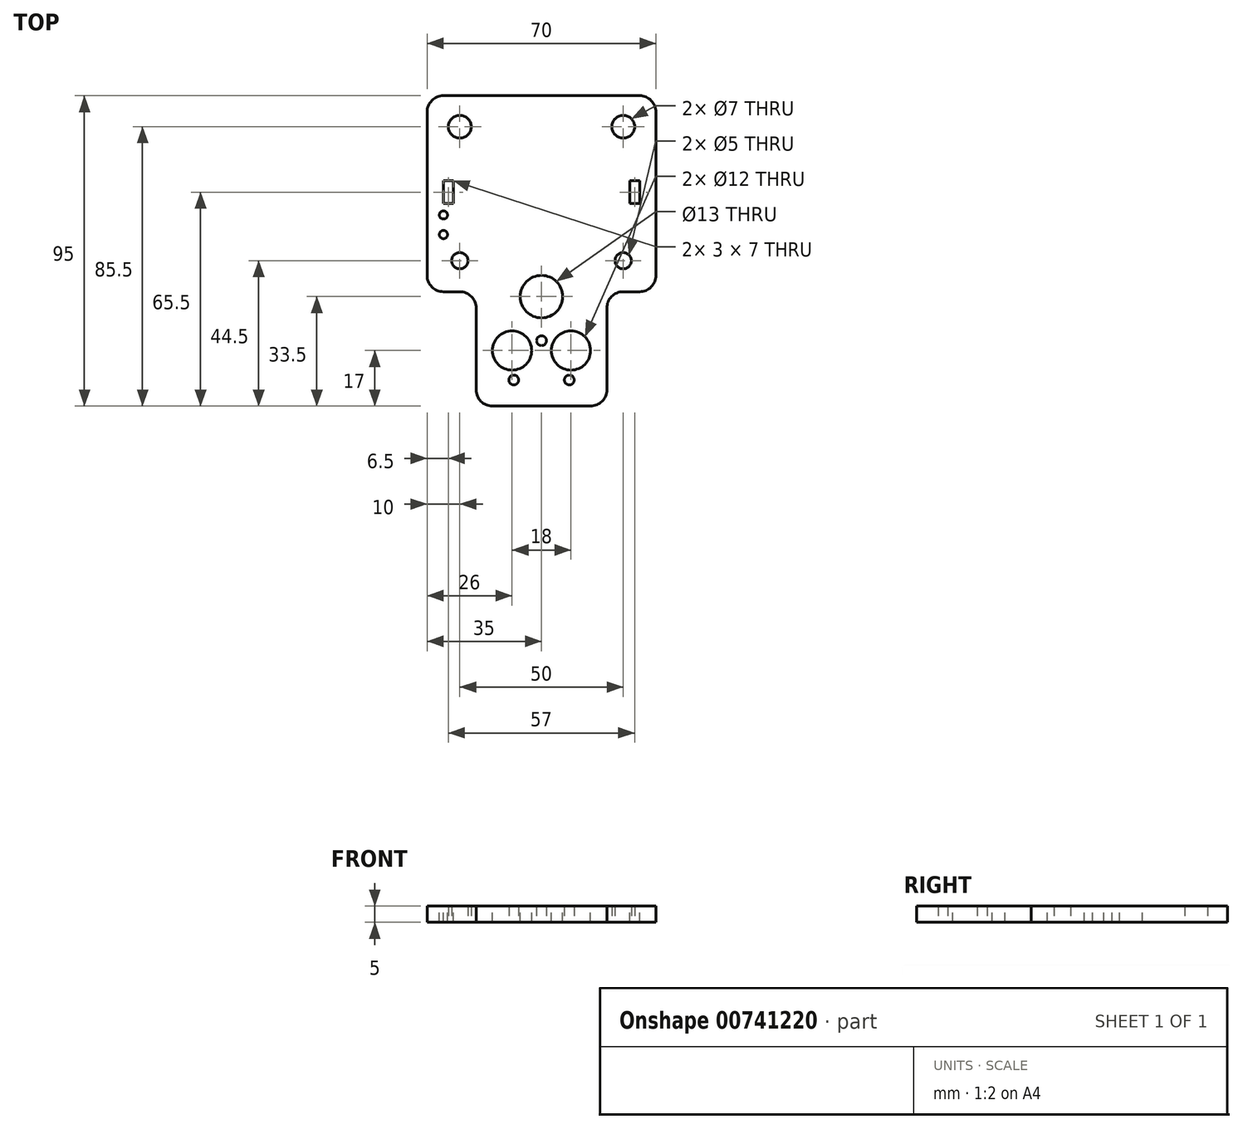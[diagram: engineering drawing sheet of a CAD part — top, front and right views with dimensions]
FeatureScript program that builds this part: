
annotation { "Feature Type Name" : "Feature", "Feature Type Description" : "" }
export const myFeature = defineFeature(function(context is Context, id is Id, definition is map)
    precondition{}
    {
        {
            var Q0;
            Q0=qCreatedBy(makeId("Top.planeOp"),FACE);
            var sketch = newSketch(context, id + "F0", { "sketchPlane" : qUnion([Q0])});
            skLineSegment(sketch, "E0.bottom", {"start": v(35, 30) * mm, "end": v(-35, 30) * mm});
            skLineSegment(sketch, "E0.top", {"start": v(35, -30) * mm, "end": v(-35, -30) * mm});
            skLineSegment(sketch, "E0.left", {"start": v(35, 30) * mm, "end": v(35, -30) * mm});
            skLineSegment(sketch, "E0.right", {"start": v(-35, 30) * mm, "end": v(-35, -30) * mm});
            skPoint(sketch, "E0.middle", {"position": v(0, 0) * mm});
            skLineSegment(sketch, "E1.bottom", {"start": v(20, -30) * mm, "end": v(-20, -30) * mm});
            skLineSegment(sketch, "E1.top", {"start": v(20, -65) * mm, "end": v(-20, -65) * mm});
            skLineSegment(sketch, "E1.left", {"start": v(20, -30) * mm, "end": v(20, -65) * mm});
            skLineSegment(sketch, "E1.right", {"start": v(-20, -30) * mm, "end": v(-20, -65) * mm});
            skPoint(sketch, "E1.middle", {"position": v(0, -47.5) * mm});
            skLineSegment(sketch, "E2.bottom", {"start": v(25, 20.5) * mm, "end": v(-25, 20.5) * mm, "construction": true});
            skLineSegment(sketch, "E2.top", {"start": v(25, -20.5) * mm, "end": v(-25, -20.5) * mm, "construction": true});
            skLineSegment(sketch, "E2.left", {"start": v(25, 20.5) * mm, "end": v(25, -20.5) * mm, "construction": true});
            skLineSegment(sketch, "E2.right", {"start": v(-25, 20.5) * mm, "end": v(-25, -20.5) * mm, "construction": true});
            skCircle(sketch, "E3", {"center": v(-25, 20.5) * mm, "radius": 3.5 * mm});
            skCircle(sketch, "E4", {"center": v(25, 20.5) * mm, "radius": 3.5 * mm});
            skCircle(sketch, "E5", {"center": v(-25, -20.5) * mm, "radius": 2.5 * mm});
            skCircle(sketch, "E6", {"center": v(25, -20.5) * mm, "radius": 2.5 * mm});
            skLineSegment(sketch, "E7", {"start": v(0, -65) * mm, "end": v(0, 30) * mm, "construction": true});
            skLineSegment(sketch, "E8", {"start": v(-20, -57) * mm, "end": v(20, -57) * mm, "construction": true});
            skCircle(sketch, "E9", {"center": v(-8.5, -57) * mm, "radius": 1.5 * mm});
            skCircle(sketch, "E10", {"center": v(8.5, -57) * mm, "radius": 1.5 * mm});
            skCircle(sketch, "E11", {"center": v(0, -45) * mm, "radius": 1.5 * mm});
            skSolve(sketch);
        }
        {
            var Q0;
            Q0 = qSketchRegion(id + "F0", true);
            extrude(context, id + "F1", {"entities" : qUnion([Q0]), "depth" : 5 * mm, "offsetDistance" : 25 * mm});
        }
        {
            var Q0;
            Q0=makeQuery(id+"F1.opExtrude","CAP_FACE",FACE,{"disambiguationData":[OSD([sQuery(id+"F0.wireOp",EDGE,"E0.bottom"),sQuery(id+"F0.wireOp",EDGE,"E0.top"),sQuery(id+"F0.wireOp",EDGE,"E0.left"),sQuery(id+"F0.wireOp",EDGE,"E0.right"),sQuery(id+"F0.wireOp",EDGE,"E1.top"),sQuery(id+"F0.wireOp",EDGE,"E1.left"),sQuery(id+"F0.wireOp",EDGE,"E1.right"),sQuery(id+"F0.wireOp",EDGE,"E3"),sQuery(id+"F0.wireOp",EDGE,"E4"),sQuery(id+"F0.wireOp",EDGE,"E5"),sQuery(id+"F0.wireOp",EDGE,"E6"),sQuery(id+"F0.wireOp",EDGE,"E9"),sQuery(id+"F0.wireOp",EDGE,"E10"),sQuery(id+"F0.wireOp",EDGE,"E11")])],"isStart":false});
            var sketch = newSketch(context, id + "F2", { "sketchPlane" : qUnion([Q0])});
            skLineSegment(sketch, "E12", {"start": v(0, 30) * mm, "end": v(0, -65) * mm, "construction": true});
            skLineSegment(sketch, "E13", {"start": v(-20, -48) * mm, "end": v(20, -48) * mm, "construction": true});
            skCircle(sketch, "E14", {"center": v(-9, -48) * mm, "radius": 6 * mm});
            skCircle(sketch, "E15", {"center": v(9, -48) * mm, "radius": 6 * mm});
            skCircle(sketch, "E16", {"center": v(0, -31.5) * mm, "radius": 6.5 * mm});
            skSolve(sketch);
        }
        {
            var Q0;
            Q0 = qSketchRegion(id + "F2", true);
            extrude(context, id + "F3", {"entities" : qUnion([Q0]), "operationType" : NewBodyOperationType.REMOVE, "endBound" : BoundingType.THROUGH_ALL, "oppositeDirection" : true, "depth" : 25 * mm, "offsetDistance" : 25 * mm});
        }
        {
            var Q0;
            Q0=makeQuery(id+"F1.opExtrude","CAP_FACE",FACE,{"disambiguationData":[OSD([sQuery(id+"F0.wireOp",EDGE,"E0.bottom"),sQuery(id+"F0.wireOp",EDGE,"E0.top"),sQuery(id+"F0.wireOp",EDGE,"E0.left"),sQuery(id+"F0.wireOp",EDGE,"E0.right"),sQuery(id+"F0.wireOp",EDGE,"E1.top"),sQuery(id+"F0.wireOp",EDGE,"E1.left"),sQuery(id+"F0.wireOp",EDGE,"E1.right"),sQuery(id+"F0.wireOp",EDGE,"E3"),sQuery(id+"F0.wireOp",EDGE,"E4"),sQuery(id+"F0.wireOp",EDGE,"E5"),sQuery(id+"F0.wireOp",EDGE,"E6"),sQuery(id+"F0.wireOp",EDGE,"E9"),sQuery(id+"F0.wireOp",EDGE,"E10"),sQuery(id+"F0.wireOp",EDGE,"E11")])],"isStart":false});
            var sketch = newSketch(context, id + "F4", { "sketchPlane" : qUnion([Q0])});
            skLineSegment(sketch, "E17.bottom", {"start": v(30, -3) * mm, "end": v(27, -3) * mm});
            skLineSegment(sketch, "E17.top", {"start": v(30, 4) * mm, "end": v(27, 4) * mm});
            skLineSegment(sketch, "E17.left", {"start": v(30, -3) * mm, "end": v(30, 4) * mm});
            skLineSegment(sketch, "E17.right", {"start": v(27, -3) * mm, "end": v(27, 4) * mm});
            skPoint(sketch, "E17.middle", {"position": v(28.5, 0.5) * mm});
            skLineSegment(sketch, "E18.bottom", {"start": v(-27, 4) * mm, "end": v(-30, 4) * mm});
            skLineSegment(sketch, "E18.top", {"start": v(-27, -3) * mm, "end": v(-30, -3) * mm});
            skLineSegment(sketch, "E18.left", {"start": v(-27, 4) * mm, "end": v(-27, -3) * mm});
            skLineSegment(sketch, "E18.right", {"start": v(-30, 4) * mm, "end": v(-30, -3) * mm});
            skPoint(sketch, "E18.middle", {"position": v(-28.5, 0.5) * mm});
            skLineSegment(sketch, "E19", {"start": v(0, 30) * mm, "end": v(0, -65) * mm, "construction": true});
            skSolve(sketch);
        }
        {
            var Q0;
            Q0 = qSketchRegion(id + "F4", true);
            extrude(context, id + "F5", {"entities" : qUnion([Q0]), "operationType" : NewBodyOperationType.REMOVE, "endBound" : BoundingType.THROUGH_ALL, "oppositeDirection" : true, "depth" : 25 * mm, "offsetDistance" : 25 * mm});
        }
        {
            var Q0;
            Q0=makeQuery(id+"F2.imprint","IMPRINT",FACE,{"disambiguationData":[TD([[makeQuery(id+"F2.imprint","IMPRINT",EDGE,{"derivedFrom":sQuery(id+"F2.wireOp",EDGE,"E14")}),-1.0]])]});
            var sketch = newSketch(context, id + "F6", { "sketchPlane" : qUnion([Q0])});
            skLineSegment(sketch, "E20", {"start": v(-30, -6.5) * mm, "end": v(-30, -12.5) * mm, "construction": true});
            skCircle(sketch, "E21", {"center": v(-30, -6.5) * mm, "radius": 1.25 * mm});
            skCircle(sketch, "E22", {"center": v(-30, -12.5) * mm, "radius": 1.25 * mm});
            skSolve(sketch);
        }
        {
            var Q0;
            Q0 = qSketchRegion(id + "F6", true);
            extrude(context, id + "F7", {"entities" : qUnion([Q0]), "operationType" : NewBodyOperationType.REMOVE, "endBound" : BoundingType.THROUGH_ALL, "oppositeDirection" : true, "depth" : 25 * mm, "offsetDistance" : 25 * mm});
        }
        {
            var Q0;
            Q0=makeQuery(id+"F1.opExtrude","SWEPT_EDGE",EDGE,{"disambiguationData":[OSD([sQuery(id+"F0.wireOp",EDGE,"E0.top"),sQuery(id+"F0.wireOp",EDGE,"E1.right")])]});
            var Q1;
            Q1=makeQuery(id+"F1.opExtrude","SWEPT_EDGE",EDGE,{"disambiguationData":[OSD([sQuery(id+"F0.wireOp",EDGE,"E1.top"),sQuery(id+"F0.wireOp",EDGE,"E1.right")])]});
            var Q2;
            Q2=makeQuery(id+"F1.opExtrude","SWEPT_EDGE",EDGE,{"disambiguationData":[OSD([sQuery(id+"F0.wireOp",EDGE,"E1.top"),sQuery(id+"F0.wireOp",EDGE,"E1.left")])]});
            var Q3;
            Q3=makeQuery(id+"F1.opExtrude","SWEPT_EDGE",EDGE,{"disambiguationData":[OSD([sQuery(id+"F0.wireOp",EDGE,"E0.top"),sQuery(id+"F0.wireOp",EDGE,"E1.left")])]});
            var Q4;
            Q4=makeQuery(id+"F1.opExtrude","SWEPT_EDGE",EDGE,{"disambiguationData":[OSD([sQuery(id+"F0.wireOp",EDGE,"E0.top"),sQuery(id+"F0.wireOp",EDGE,"E0.left")])]});
            var Q5;
            Q5=makeQuery(id+"F1.opExtrude","SWEPT_EDGE",EDGE,{"disambiguationData":[OSD([sQuery(id+"F0.wireOp",EDGE,"E0.bottom"),sQuery(id+"F0.wireOp",EDGE,"E0.left")])]});
            var Q6;
            Q6=makeQuery(id+"F1.opExtrude","SWEPT_EDGE",EDGE,{"disambiguationData":[OSD([sQuery(id+"F0.wireOp",EDGE,"E0.bottom"),sQuery(id+"F0.wireOp",EDGE,"E0.right")])]});
            var Q7;
            Q7=makeQuery(id+"F1.opExtrude","SWEPT_EDGE",EDGE,{"disambiguationData":[OSD([sQuery(id+"F0.wireOp",EDGE,"E0.top"),sQuery(id+"F0.wireOp",EDGE,"E0.right")])]});
            fillet(context, id + "F8", {"entities" : qUnion([Q0, Q1, Q2, Q3, Q4, Q5, Q6, Q7]), "tangentPropagation" : true, "radius" : 5 * mm, "defaultsChanged" : false, "vertexSettings" : [], "allowEdgeOverflow" : false});
        }
    });
